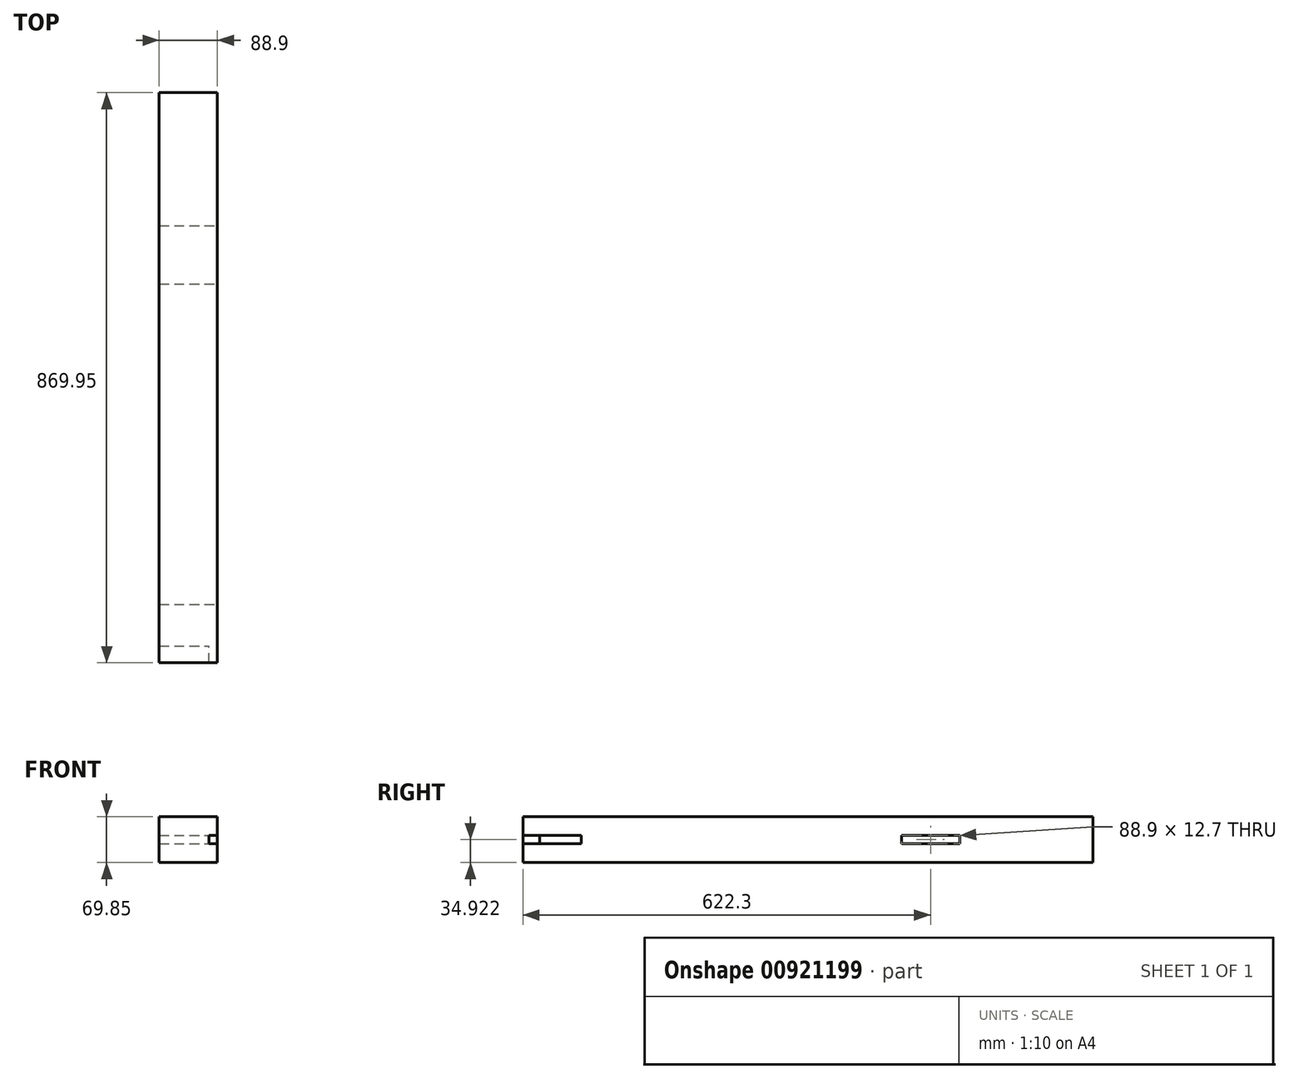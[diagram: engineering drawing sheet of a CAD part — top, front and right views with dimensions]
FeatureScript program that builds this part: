
annotation { "Feature Type Name" : "Feature", "Feature Type Description" : "" }
export const myFeature = defineFeature(function(context is Context, id is Id, definition is map)
    precondition{}
    {
        {
            var Q0;
            Q0=qCreatedBy(makeId("Front.planeOp"),FACE);
            var sketch = newSketch(context, id + "F0", { "sketchPlane" : qUnion([Q0])});
            skLineSegment(sketch, "E0.bottom", {"start": v(0, -11.04) * mm, "end": v(88.9, -11.04) * mm});
            skLineSegment(sketch, "E0.top", {"start": v(0, 58.8) * mm, "end": v(88.9, 58.8) * mm});
            skLineSegment(sketch, "E0.left", {"start": v(0, -11.04) * mm, "end": v(0, 58.8) * mm});
            skLineSegment(sketch, "E0.right", {"start": v(88.9, -11.04) * mm, "end": v(88.9, 58.8) * mm});
            skSolve(sketch);
        }
        {
            var Q0;
            Q0 = qSketchRegion(id + "F0", true);
            extrude(context, id + "F1", {"entities" : qUnion([Q0]), "depth" : 869.95 * mm, "offsetDistance" : 25.4 * mm});
        }
        {
            var Q0;
            Q0=makeQuery(id+"F1.opExtrude","SWEPT_FACE",FACE,{"disambiguationData":[OSD([sQuery(id+"F0.wireOp",EDGE,"E0.right")])]});
            var sketch = newSketch(context, id + "F2", { "sketchPlane" : qUnion([Q0])});
            skLineSegment(sketch, "E1.bottom", {"start": v(-869.95, 17.53) * mm, "end": v(-844.55, 17.53) * mm});
            skLineSegment(sketch, "E1.top", {"start": v(-869.95, 30.23) * mm, "end": v(-844.55, 30.23) * mm});
            skLineSegment(sketch, "E1.left", {"start": v(-869.95, 17.53) * mm, "end": v(-869.95, 30.23) * mm});
            skLineSegment(sketch, "E1.right", {"start": v(-844.55, 17.53) * mm, "end": v(-844.55, 30.23) * mm});
            skLineSegment(sketch, "E2", {"start": v(-869.95, 23.88) * mm, "end": v(0, 23.88) * mm, "construction": true});
            skSolve(sketch);
        }
        {
            var Q0;
            Q0 = qSketchRegion(id + "F2", true);
            extrude(context, id + "F3", {"entities" : qUnion([Q0]), "operationType" : NewBodyOperationType.REMOVE, "oppositeDirection" : true, "depth" : 12.7 * mm, "offsetDistance" : 25.4 * mm});
        }
        {
            var Q0;
            Q0=makeQuery(id+"F1.opExtrude","SWEPT_FACE",FACE,{"disambiguationData":[OSD([sQuery(id+"F0.wireOp",EDGE,"E0.right")])]});
            var sketch = newSketch(context, id + "F4", { "sketchPlane" : qUnion([Q0])});
            skLineSegment(sketch, "E3.bottom", {"start": v(-844.55, 17.53) * mm, "end": v(-781.05, 17.53) * mm});
            skLineSegment(sketch, "E3.top", {"start": v(-844.55, 30.23) * mm, "end": v(-781.05, 30.23) * mm});
            skLineSegment(sketch, "E3.left", {"start": v(-844.55, 17.53) * mm, "end": v(-844.55, 30.23) * mm});
            skLineSegment(sketch, "E3.right", {"start": v(-781.05, 17.53) * mm, "end": v(-781.05, 30.23) * mm});
            skSolve(sketch);
        }
        {
            var Q0;
            Q0 = qSketchRegion(id + "F4", true);
            var Q1;
            Q1=makeQuery(id+"F1.opExtrude","SWEPT_FACE",FACE,{"disambiguationData":[OSD([sQuery(id+"F0.wireOp",EDGE,"E0.left")])]});
            extrude(context, id + "F5", {"entities" : qUnion([Q0]), "operationType" : NewBodyOperationType.REMOVE, "endBound" : BoundingType.UP_TO_SURFACE, "oppositeDirection" : true, "depth" : 88.9 * mm, "endBoundEntityFace" : qUnion([Q1]), "offsetDistance" : 25.4 * mm});
        }
        {
            var Q0;
            Q0=makeQuery(id+"F1.opExtrude","SWEPT_FACE",FACE,{"disambiguationData":[OSD([sQuery(id+"F0.wireOp",EDGE,"E0.right")])]});
            var sketch = newSketch(context, id + "F6", { "sketchPlane" : qUnion([Q0])});
            skLineSegment(sketch, "E4.bottom", {"start": v(-292.1, 17.53) * mm, "end": v(-203.2, 17.53) * mm});
            skLineSegment(sketch, "E4.top", {"start": v(-292.1, 30.23) * mm, "end": v(-203.2, 30.23) * mm});
            skLineSegment(sketch, "E4.left", {"start": v(-292.1, 17.53) * mm, "end": v(-292.1, 30.23) * mm});
            skLineSegment(sketch, "E4.right", {"start": v(-203.2, 17.53) * mm, "end": v(-203.2, 30.23) * mm});
            skLineSegment(sketch, "E5", {"start": v(0, 23.88) * mm, "end": v(-781.05, 23.88) * mm, "construction": true});
            skSolve(sketch);
        }
        {
            var Q0;
            Q0 = qSketchRegion(id + "F6", true);
            var Q1;
            Q1=makeQuery(id+"F1.opExtrude","SWEPT_FACE",FACE,{"disambiguationData":[OSD([sQuery(id+"F0.wireOp",EDGE,"E0.left")])]});
            extrude(context, id + "F7", {"entities" : qUnion([Q0]), "operationType" : NewBodyOperationType.REMOVE, "endBound" : BoundingType.UP_TO_SURFACE, "oppositeDirection" : true, "depth" : 25.4 * mm, "endBoundEntityFace" : qUnion([Q1]), "offsetDistance" : 25.4 * mm});
        }
    });
